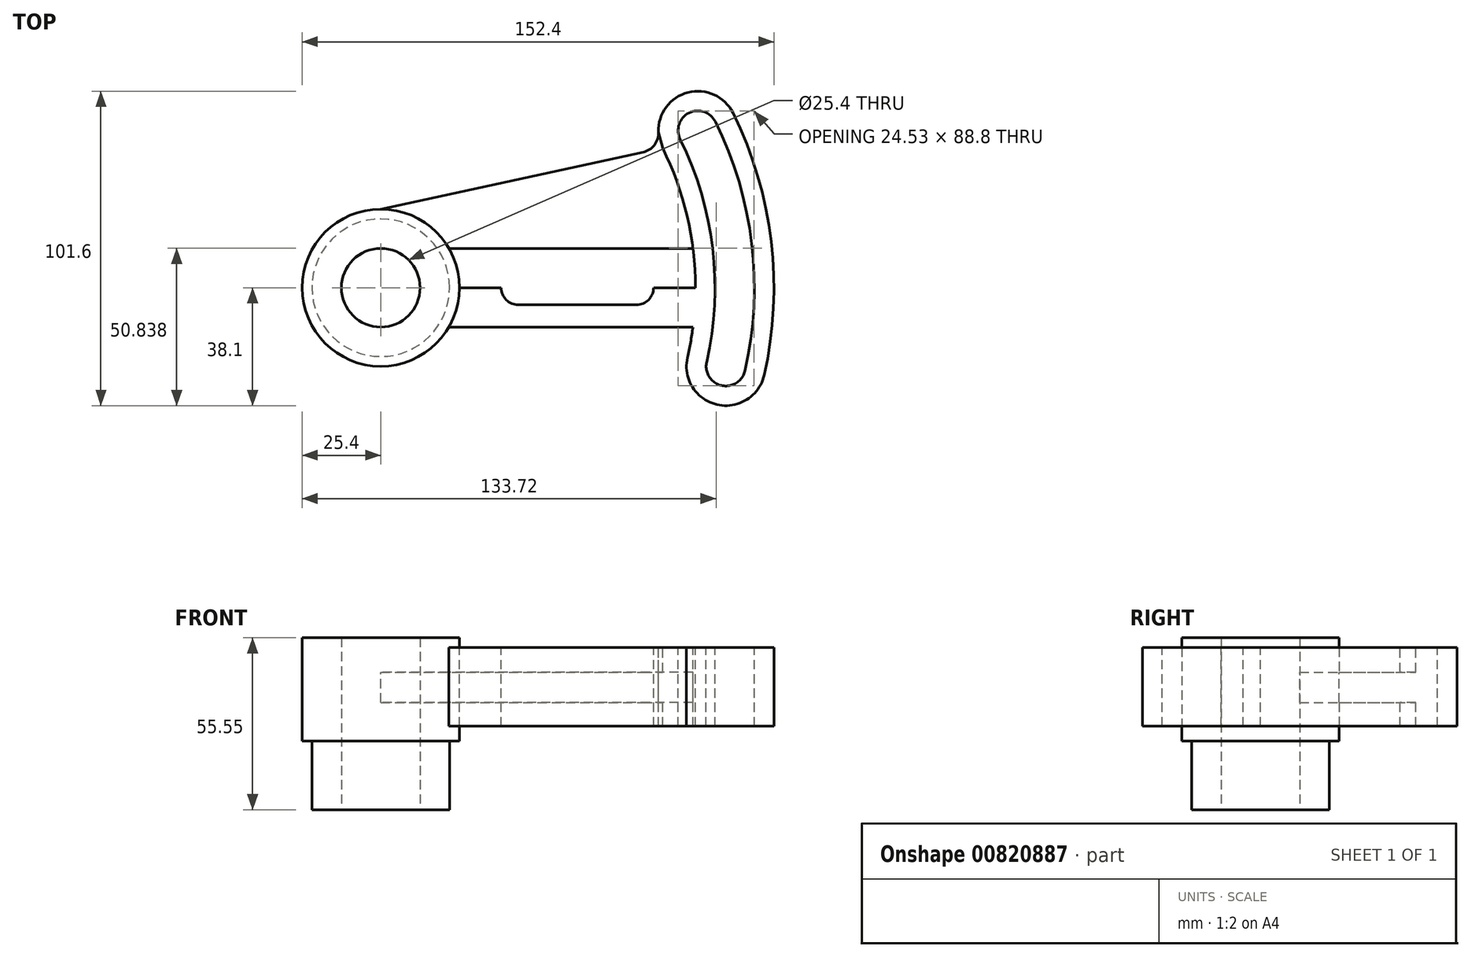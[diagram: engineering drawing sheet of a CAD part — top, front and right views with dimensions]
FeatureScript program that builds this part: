
annotation { "Feature Type Name" : "Feature", "Feature Type Description" : "" }
export const myFeature = defineFeature(function(context is Context, id is Id, definition is map)
    precondition{}
    {
        {
            var Q0;
            Q0=qCreatedBy(makeId("Top.planeOp"),FACE);
            var sketch = newSketch(context, id + "F0", { "sketchPlane" : qUnion([Q0])});
            skLineSegment(sketch, "E0", {"start": v(0, 0) * mm, "end": v(-44.45, 0) * mm});
            skLineSegment(sketch, "E1", {"start": v(38.1, 0) * mm, "end": v(63.5, 0) * mm});
            skCircle(sketch, "E2", {"center": v(-44.45, 0) * mm, "radius": 12.7 * mm});
            skCircle(sketch, "E3", {"center": v(-44.45, 0) * mm, "radius": 22.23 * mm});
            skCircle(sketch, "E4", {"center": v(-44.45, 0) * mm, "radius": 25.4 * mm});
            skLineSegment(sketch, "E5", {"start": v(0, 0) * mm, "end": v(0, 12.7) * mm});
            skLineSegment(sketch, "E6", {"start": v(0, 12.7) * mm, "end": v(0, 5.55) * mm});
            skLineSegment(sketch, "E7", {"start": v(0, -12.7) * mm, "end": v(-22.45, -12.7) * mm});
            skLineSegment(sketch, "E8", {"start": v(0, 12.7) * mm, "end": v(-22.45, 12.7) * mm});
            skArc(sketch, "E9", {"start": v(0, 5.55) * mm, "mid": v(-5.55, 0) * mm, "end": v(0, -5.55) * mm});
            skArc(sketch, "E10", {"start": v(38.1, -5.55) * mm, "mid": v(43.65, 0) * mm, "end": v(38.1, 5.55) * mm});
            skLineSegment(sketch, "E11", {"start": v(0, -5.55) * mm, "end": v(38.1, -5.55) * mm});
            skLineSegment(sketch, "E12", {"start": v(0, 5.55) * mm, "end": v(38.1, 5.55) * mm});
            skLineSegment(sketch, "E13.trimOffspring", {"start": v(0, -5.55) * mm, "end": v(0, -12.7) * mm});
            skArc(sketch, "E14", {"start": v(63.63, 53.62) * mm, "mid": v(55.12, 56.49) * mm, "end": v(52.25, 47.98) * mm});
            skArc(sketch, "E15", {"start": v(60.8, -23.99) * mm, "mid": v(65.58, -31.6) * mm, "end": v(73.18, -26.81) * mm});
            skArc(sketch, "E16", {"start": v(60.8, -23.99) * mm, "mid": v(62.75, 12.73) * mm, "end": v(52.25, 47.98) * mm});
            skArc(sketch, "E17", {"start": v(73.18, -26.81) * mm, "mid": v(75.36, 14.23) * mm, "end": v(63.63, 53.62) * mm});
            skArc(sketch, "E18", {"start": v(54.6, -22.58) * mm, "mid": v(56.44, 11.98) * mm, "end": v(46.56, 45.16) * mm});
            skArc(sketch, "E19", {"start": v(79.37, -28.22) * mm, "mid": v(81.66, 14.98) * mm, "end": v(69.32, 56.44) * mm});
            skArc(sketch, "E20", {"start": v(54.6, -22.58) * mm, "mid": v(64.17, -37.78) * mm, "end": v(79.37, -28.22) * mm});
            skArc(sketch, "E21.trimOffspring", {"start": v(69.32, 56.44) * mm, "mid": v(54.78, 63.1) * mm, "end": v(45.25, 50.26) * mm});
            skLineSegment(sketch, "E22", {"start": v(0, 12.7) * mm, "end": v(56.35, 12.7) * mm});
            skLineSegment(sketch, "E23", {"start": v(0, -12.7) * mm, "end": v(56.35, -12.7) * mm});
            skLineSegment(sketch, "E24", {"start": v(-44.45, 0) * mm, "end": v(-44.45, 25.4) * mm});
            skLineSegment(sketch, "E25", {"start": v(-44.45, 25.4) * mm, "end": v(40.25, 43.79) * mm});
            skPoint(sketch, "E26.visualSharp", {"position": v(46.56, 45.16) * mm});
            skArc(sketch, "E26.filletArc", {"start": v(40.25, 43.79) * mm, "mid": v(43.93, 46.11) * mm, "end": v(45.25, 50.26) * mm});
            skLineSegment(sketch, "E27", {"start": v(45.25, 50.26) * mm, "end": v(46.56, 45.16) * mm});
            skSolve(sketch);
        }
        {
            var Q0;
            {var subQ0=sQuery(id+"F0.wireOp",EDGE,"E4");var subQ4=sQuery(id+"F0.wireOp",EDGE,"E0");var subQ5=makeQuery(id+"F0.imprint","INTERSECT",VERTEX,{"derivedFrom":[subQ4,subQ0]});Q0=makeQuery(id+"F0.imprint","IMPRINT",FACE,{"disambiguationData":[TD([[makeQuery(id+"F0.imprint","IMPRINT",EDGE,{"disambiguationData":[TD([[subQ5,-1.0]])],"derivedFrom":subQ4}),-1.0]])]});}
            var Q1;
            {var subQ0=sQuery(id+"F0.wireOp",EDGE,"E4");var subQ2=sQuery(id+"F0.wireOp",EDGE,"E0");var subQ3=makeQuery(id+"F0.imprint","INTERSECT",VERTEX,{"derivedFrom":[subQ2,subQ0]});Q1=makeQuery(id+"F0.imprint","IMPRINT",FACE,{"disambiguationData":[TD([[makeQuery(id+"F0.imprint","IMPRINT",EDGE,{"disambiguationData":[TD([[subQ3,-1.0]])],"derivedFrom":subQ2}),1.0]])]});}
            var Q2;
            {var subQ0=sQuery(id+"F0.wireOp",EDGE,"E3");var subQ1=sQuery(id+"F0.wireOp",EDGE,"E0");var subQ2=makeQuery(id+"F0.imprint","INTERSECT",VERTEX,{"derivedFrom":[subQ1,subQ0]});Q2=makeQuery(id+"F0.imprint","IMPRINT",FACE,{"disambiguationData":[TD([[makeQuery(id+"F0.imprint","IMPRINT",EDGE,{"disambiguationData":[TD([[subQ2,-1.0]])],"derivedFrom":subQ1}),1.0]])]});}
            var Q3;
            {var subQ0=sQuery(id+"F0.wireOp",EDGE,"E3");var subQ1=sQuery(id+"F0.wireOp",EDGE,"E0");var subQ2=makeQuery(id+"F0.imprint","INTERSECT",VERTEX,{"derivedFrom":[subQ1,subQ0]});Q3=makeQuery(id+"F0.imprint","IMPRINT",FACE,{"disambiguationData":[TD([[makeQuery(id+"F0.imprint","IMPRINT",EDGE,{"disambiguationData":[TD([[subQ2,-1.0]])],"derivedFrom":subQ1}),-1.0]])]});}
            extrude(context, id + "F1", {"entities" : qUnion([Q0, Q1, Q2, Q3]), "depth" : 3.17 * mm, "offsetDistance" : 25.4 * mm, "hasSecondDirection" : true, "secondDirectionOppositeDirection" : true, "secondDirectionDepth" : 30.15 * mm});
        }
        {
            var Q0;
            {var subQ6=sQuery(id+"F0.wireOp",EDGE,"E14");Q0=makeQuery(id+"F0.imprint","IMPRINT",FACE,{"disambiguationData":[TD([[makeQuery(id+"F0.imprint","IMPRINT",EDGE,{"derivedFrom":subQ6}),-1.0]])]});}
            extrude(context, id + "F2", {"entities" : qUnion([Q0]), "operationType" : NewBodyOperationType.ADD, "oppositeDirection" : true, "depth" : 25.4 * mm, "offsetDistance" : 25.4 * mm});
        }
        {
            var Q0;
            {var subQ4=sQuery(id+"F0.wireOp",EDGE,"E7");Q0=makeQuery(id+"F0.imprint","IMPRINT",FACE,{"disambiguationData":[TD([[makeQuery(id+"F0.imprint","IMPRINT",EDGE,{"derivedFrom":subQ4}),-1.0]])]});}
            var Q1;
            {var subQ1=sQuery(id+"F0.wireOp",EDGE,"E6");Q1=makeQuery(id+"F0.imprint","IMPRINT",FACE,{"disambiguationData":[TD([[makeQuery(id+"F0.imprint","IMPRINT",EDGE,{"derivedFrom":subQ1}),-1.0]])]});}
            var Q2;
            Q2=makeQuery(id+"F0.imprint","IMPRINT",FACE,{"disambiguationData":[TD([[makeQuery(id+"F0.imprint","IMPRINT",EDGE,{"derivedFrom":sQuery(id+"F0.wireOp",EDGE,"E6")}),1.0]])]});
            var Q3;
            {var subQ0=sQuery(id+"F0.wireOp",EDGE,"E11");Q3=makeQuery(id+"F0.imprint","IMPRINT",FACE,{"disambiguationData":[TD([[makeQuery(id+"F0.imprint","IMPRINT",EDGE,{"derivedFrom":subQ0}),-1.0]])]});}
            extrude(context, id + "F3", {"entities" : qUnion([Q0, Q1, Q2, Q3]), "operationType" : NewBodyOperationType.ADD, "oppositeDirection" : true, "depth" : 25.4 * mm, "offsetDistance" : 25.4 * mm});
        }
        {
            var Q0;
            {var subQ3=sQuery(id+"F0.wireOp",EDGE,"E8");Q0=makeQuery(id+"F0.imprint","IMPRINT",FACE,{"disambiguationData":[TD([[makeQuery(id+"F0.imprint","IMPRINT",EDGE,{"derivedFrom":subQ3}),-1.0]])]});}
            extrude(context, id + "F4", {"entities" : qUnion([Q0]), "operationType" : NewBodyOperationType.ADD, "oppositeDirection" : true, "depth" : 17.75 * mm, "offsetDistance" : 25.4 * mm, "hasSecondDirection" : true, "secondDirectionOppositeDirection" : true, "secondDirectionDepth" : 7.92 * mm});
        }
        {
            var Q0;
            {var subQ0=sQuery(id+"F0.wireOp",EDGE,"E3");var subQ1=sQuery(id+"F0.wireOp",EDGE,"E0");var subQ2=makeQuery(id+"F0.imprint","INTERSECT",VERTEX,{"derivedFrom":[subQ1,subQ0]});Q0=makeQuery(id+"F0.imprint","IMPRINT",FACE,{"disambiguationData":[TD([[makeQuery(id+"F0.imprint","IMPRINT",EDGE,{"disambiguationData":[TD([[subQ2,-1.0]])],"derivedFrom":subQ1}),1.0]])]});}
            var Q1;
            {var subQ0=sQuery(id+"F0.wireOp",EDGE,"E3");var subQ1=sQuery(id+"F0.wireOp",EDGE,"E0");var subQ2=makeQuery(id+"F0.imprint","INTERSECT",VERTEX,{"derivedFrom":[subQ1,subQ0]});Q1=makeQuery(id+"F0.imprint","IMPRINT",FACE,{"disambiguationData":[TD([[makeQuery(id+"F0.imprint","IMPRINT",EDGE,{"disambiguationData":[TD([[subQ2,-1.0]])],"derivedFrom":subQ1}),-1.0]])]});}
            extrude(context, id + "F5", {"entities" : qUnion([Q0, Q1]), "operationType" : NewBodyOperationType.ADD, "oppositeDirection" : true, "depth" : 52.37 * mm, "offsetDistance" : 25.4 * mm});
        }
    });
